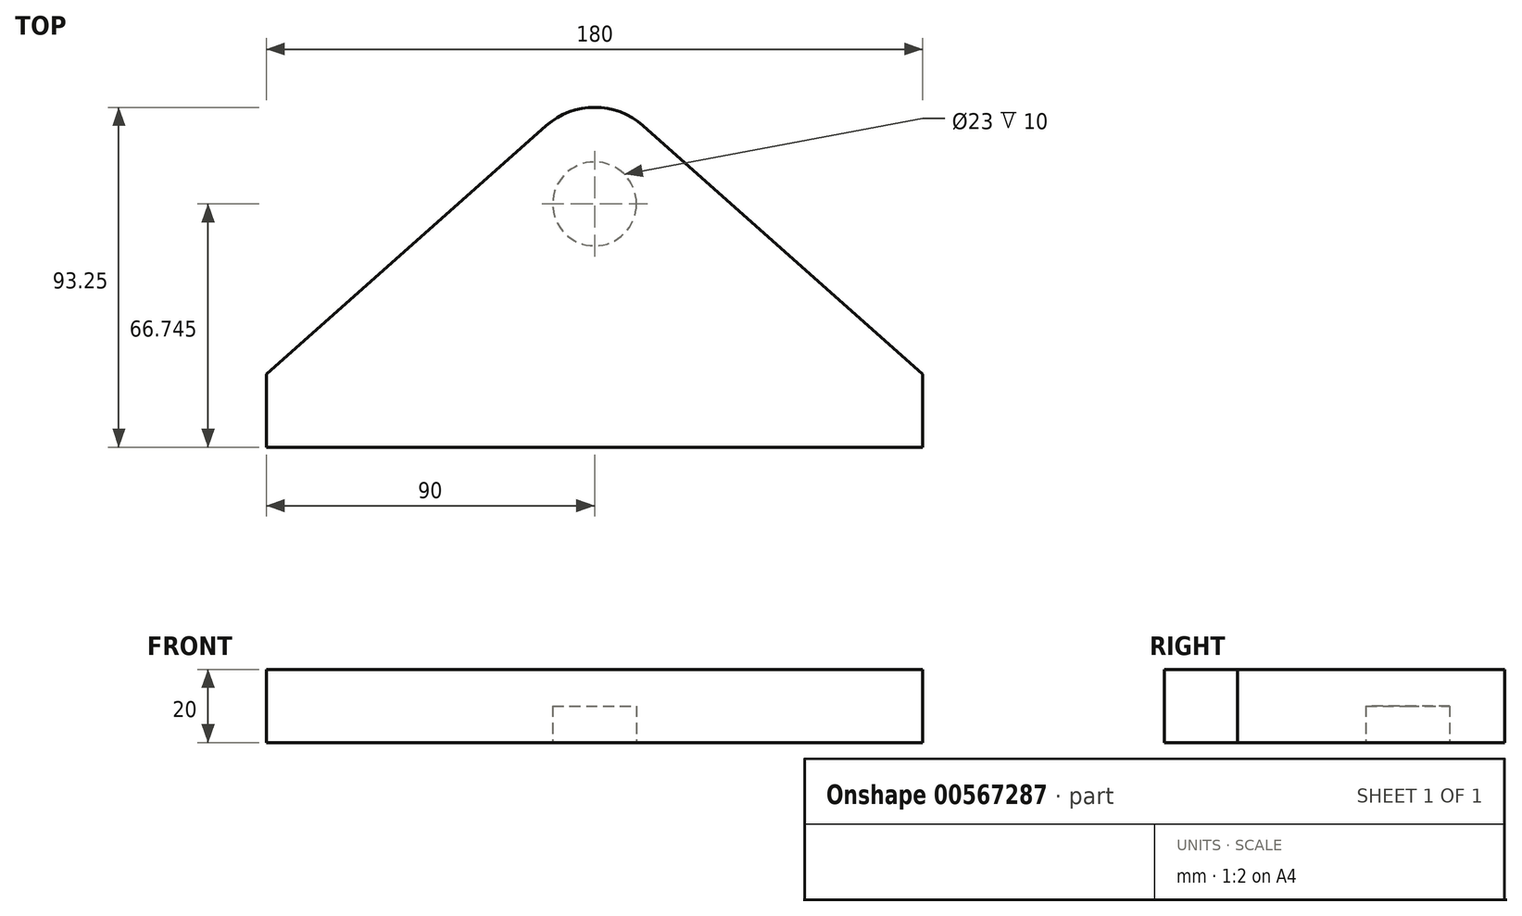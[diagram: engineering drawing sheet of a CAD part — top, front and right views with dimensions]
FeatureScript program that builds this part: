
annotation { "Feature Type Name" : "Feature", "Feature Type Description" : "" }
export const myFeature = defineFeature(function(context is Context, id is Id, definition is map)
    precondition{}
    {
        {
            var Q0;
            Q0=qCreatedBy(makeId("Top.planeOp"),FACE);
            var sketch = newSketch(context, id + "F0", { "sketchPlane" : qUnion([Q0])});
            skLineSegment(sketch, "E0.bottom", {"start": v(-112.55, 59.5) * mm, "end": v(67.45, 59.5) * mm});
            skLineSegment(sketch, "E0.top", {"start": v(-112.55, -40.5) * mm, "end": v(67.45, -40.5) * mm});
            skLineSegment(sketch, "E0.left", {"start": v(-112.55, 59.5) * mm, "end": v(-112.55, -40.5) * mm});
            skLineSegment(sketch, "E0.right", {"start": v(67.45, 59.5) * mm, "end": v(67.45, -40.5) * mm});
            skLineSegment(sketch, "E1", {"start": v(-112.55, -40.5) * mm, "end": v(-112.55, -20.5) * mm});
            skLineSegment(sketch, "E2", {"start": v(67.45, -40.5) * mm, "end": v(67.45, -20.5) * mm});
            skLineSegment(sketch, "E3", {"start": v(-112.55, 59.5) * mm, "end": v(-22.55, 59.5) * mm});
            skLineSegment(sketch, "E4", {"start": v(-112.55, -20.5) * mm, "end": v(-35.84, 47.7) * mm});
            skLineSegment(sketch, "E5", {"start": v(-9.26, 47.7) * mm, "end": v(67.45, -20.5) * mm});
            skPoint(sketch, "E6.visualSharp", {"position": v(-22.55, 59.5) * mm});
            skArc(sketch, "E6.filletArc", {"start": v(-9.26, 47.7) * mm, "mid": v(-22.55, 52.75) * mm, "end": v(-35.84, 47.7) * mm});
            skSolve(sketch);
        }
        {
            var Q0;
            Q0=makeQuery(id+"F0.imprint","IMPRINT",FACE,{"disambiguationData":[TD([[makeQuery(id+"F0.imprint","IMPRINT",EDGE,{"derivedFrom":sQuery(id+"F0.wireOp",EDGE,"E0.top")}),1.0]])]});
            extrude(context, id + "F1", {"entities" : qUnion([Q0]), "depth" : 20 * mm, "offsetDistance" : 25 * mm});
        }
        {
            var Q0;
            Q0=makeQuery(id+"F1.opExtrude","CAP_FACE",FACE,{"disambiguationData":[OSD([sQuery(id+"F0.wireOp",EDGE,"E0.top"),sQuery(id+"F0.wireOp",EDGE,"E1"),sQuery(id+"F0.wireOp",EDGE,"E2"),sQuery(id+"F0.wireOp",EDGE,"E4"),sQuery(id+"F0.wireOp",EDGE,"E5"),sQuery(id+"F0.wireOp",EDGE,"E6.filletArc")])],"isStart":true});
            var sketch = newSketch(context, id + "F2", { "sketchPlane" : qUnion([Q0])});
            skCircle(sketch, "E7", {"center": v(-22.55, -26.25) * mm, "radius": 11.5 * mm});
            skSolve(sketch);
        }
        {
            var Q0;
            Q0=makeQuery(id+"F2.imprint","IMPRINT",FACE,{"disambiguationData":[TD([[makeQuery(id+"F2.imprint","IMPRINT",EDGE,{"derivedFrom":sQuery(id+"F2.wireOp",EDGE,"E7")}),1.0]])]});
            extrude(context, id + "F3", {"entities" : qUnion([Q0]), "operationType" : NewBodyOperationType.REMOVE, "oppositeDirection" : true, "depth" : 10 * mm, "offsetDistance" : 25 * mm});
        }
    });
